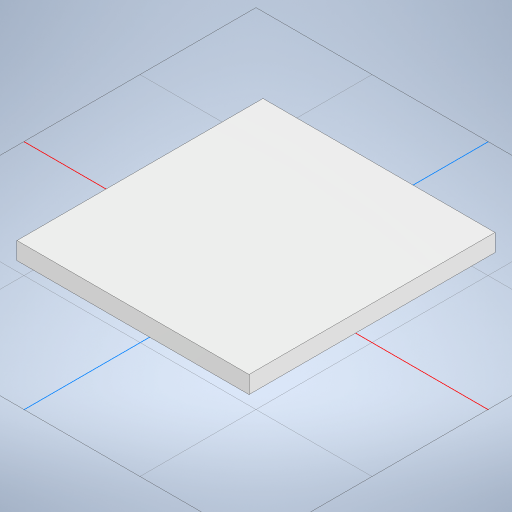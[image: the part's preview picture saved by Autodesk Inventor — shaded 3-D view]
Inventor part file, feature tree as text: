
AUTODESK INVENTOR PART (.ipt)
format: ipt  version: 2023 (Build 270158000, 158)  size: 513,536 bytes
history: native  units: mm
features: move_body x4, sketch x3, extrude x3, plane x3, mirror x2, fillet x2
ambient origin geometry x8: Origin, YZ Plane, XZ Plane, XY Plane, X Axis, Y Axis, Z Axis, Center Point
bodies: Volumenkörper1 (feature_tree)
feature tree (17):
  sketch  "Skizze3"  dims[d2=3.0mm d3=35.0mm d4=0.0mm]
  extrude  "Extrusion1"  Depth=35.0mm TaperAngle=0.0deg
  sketch  "Skizze5"  dims[d6=1.5mm d7=0.2mm d8=0.2mm d9=10.0mm]
  sketch  "Skizze7"  dims[d10=5.0mm d11=4.8mm d12=0.0mm d14=15.0mm d15=0.5mm d16=0.2mm d17=5.0mm d18=0.0mm d19=42.4mm d20=180.0deg d21=90.0deg d22=-20.0mm d23=-10.0mm d24=0.0mm d25=0.0mm d26=0.0mm d27=5.0mm]
  plane  "Arbeitsebene1"
  plane  "Arbeitsebene2"
  extrude  "Extrusion2"  Depth=0.2mm
  plane  "Arbeitsebene4"
  mirror  "Spiegeln1"
  fillet  "Rundung1"  Radius=0.2mm
  mirror  "Spiegeln2"
  fillet  "Rundung2"  Radius=10.0mm
  extrude  "Extrusion3"  Depth=5.0mm TaperAngle=0.0deg
  move_body  "Move Body1"
  move_body  "Move Body2"
  move_body  "Move Body3"
  move_body  "Move Body4"
